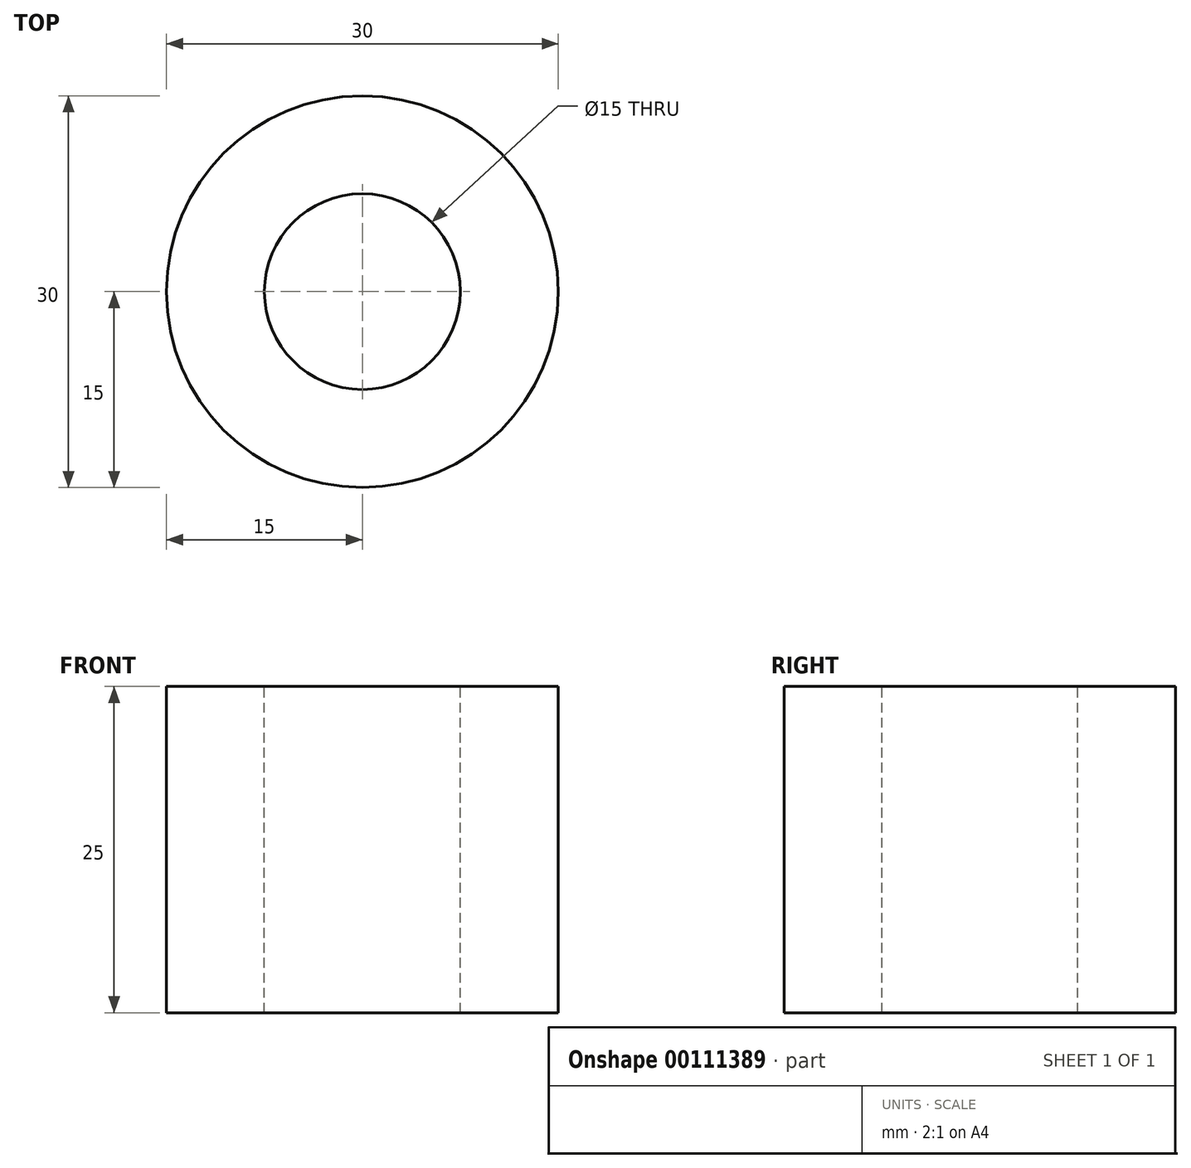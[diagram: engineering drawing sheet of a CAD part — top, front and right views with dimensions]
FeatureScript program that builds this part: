
annotation { "Feature Type Name" : "Feature", "Feature Type Description" : "" }
export const myFeature = defineFeature(function(context is Context, id is Id, definition is map)
    precondition{}
    {
        {
            var Q0;
            Q0=qCreatedBy(makeId("Front.planeOp"),FACE);
            var sketch = newSketch(context, id + "F0", { "sketchPlane" : qUnion([Q0])});
            skLineSegment(sketch, "E0.bottom", {"start": v(7.5, 0) * mm, "end": v(15, 0) * mm});
            skLineSegment(sketch, "E0.top", {"start": v(7.5, 25) * mm, "end": v(15, 25) * mm});
            skLineSegment(sketch, "E0.left", {"start": v(7.5, 0) * mm, "end": v(7.5, 25) * mm});
            skLineSegment(sketch, "E0.right", {"start": v(15, 0) * mm, "end": v(15, 25) * mm});
            skLineSegment(sketch, "E1", {"start": v(0, 35.01) * mm, "end": v(0, -18.36) * mm, "construction": true});
            skText(sketch, "E2", { "text": "6 x delrin", "fontName": "OpenSans-Regular.ttf"});
            const initialGuessF0  = {"E2": [0.00455, 0.04056, 1, 0, 0.00693]};
            skSetInitialGuess(sketch, initialGuessF0);
            skSolve(sketch);
        }
        {
            var Q0;
            Q0=makeQuery(id+"F0.imprint","IMPRINT",FACE,{"disambiguationData":[TD([[makeQuery(id+"F0.imprint","IMPRINT",EDGE,{"derivedFrom":sQuery(id+"F0.wireOp",EDGE,"E0.bottom")}),1.0]])]});
            var Q1;
            Q1=sQuery(id+"F0.wireOp",EDGE,"E1");
            revolve(context, id + "F1", {"entities" : qUnion([Q0]), "axis" : qUnion([Q1]), "revolveType" : RevolveType.FULL});
        }
    });
